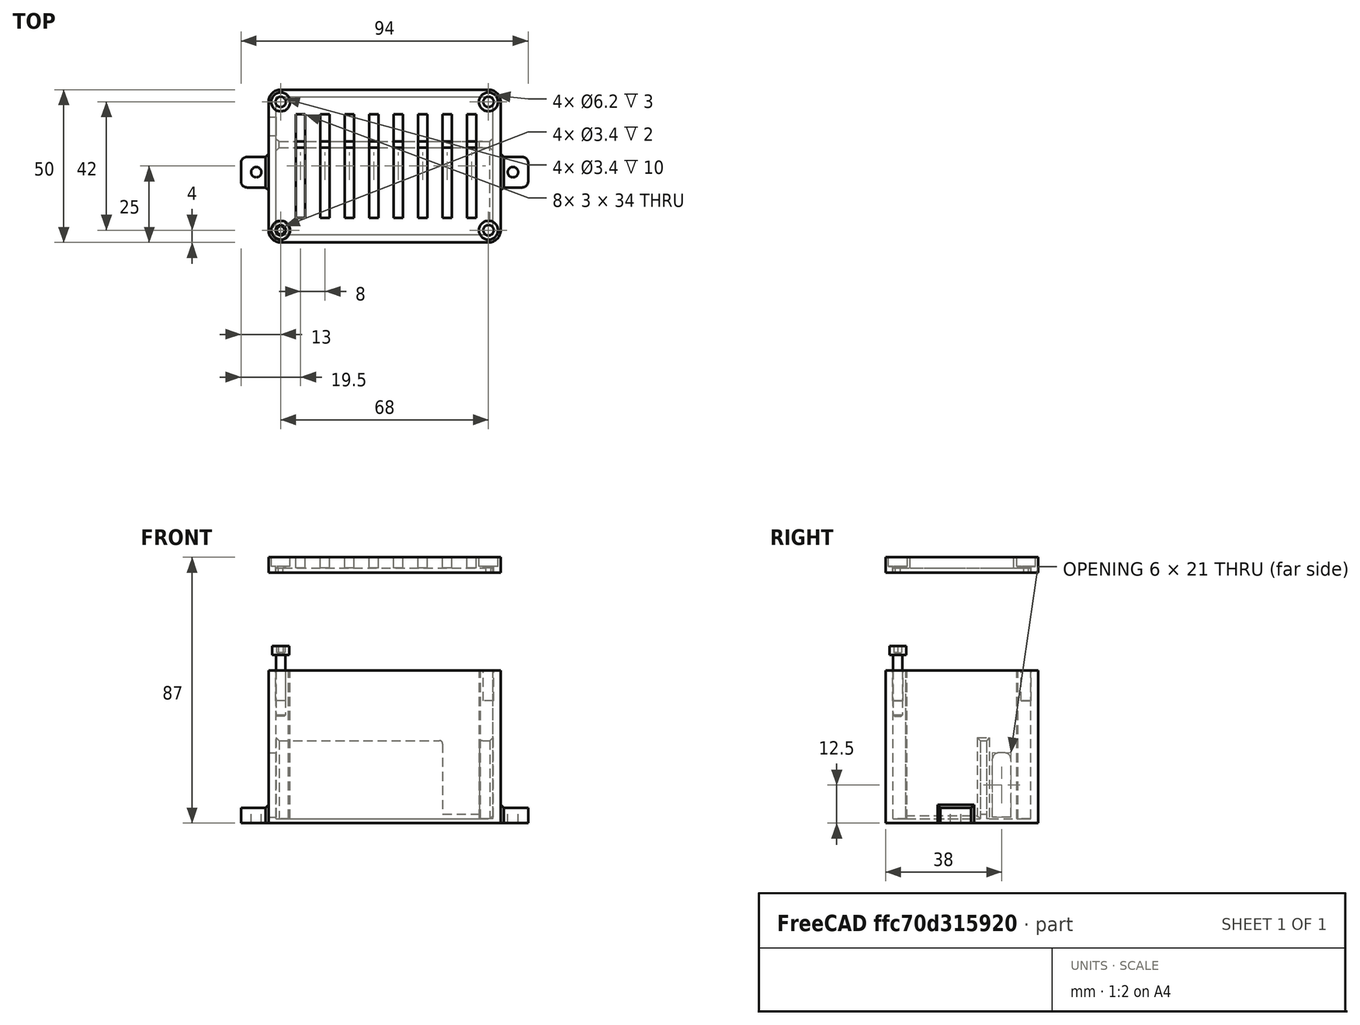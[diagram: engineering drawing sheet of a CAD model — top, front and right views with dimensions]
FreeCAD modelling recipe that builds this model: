
FCSTD DOCUMENT  (FreeCAD 0.17R12831 (Git))
Label: arbol_deseos_caja
License: All rights reserved
LicenseURL: http://es.wikipedia.org/wiki/Todos_los_derechos_reservados
objects: Part::Cylinder×18, Part::Box×17, Part::Cut×10, Part::MultiFuse×7, Part::Chamfer×4, Part::Fillet×3
note: 59 computed .brp shape members not serialized (recipe doc carries the construction recipe); baked Part::Feature solids carry a one-line shape summary decoded from their .brp

FEATURE [Part::Box] Box  label="caja exterior"
  AttacherType = Attacher::AttachEngine3D
  Height = 50
  Length = 76
  Placement = pos=(-1,-1,0) rot=(0,0,1;0rad)
  Width = 50
FEATURE [Part::Box] Box001  label="vaciado interior"
  AttacherType = Attacher::AttachEngine3D
  Height = 50
  Length = 71
  Placement = pos=(1.5,1.5,1.5) rot=(0,0,1;0rad)
  Width = 45
FEATURE [Part::Cut] Cut  label="parte inferior"
  Base = -> Box
  Tool = -> Box001
FEATURE [Part::Cylinder] Cylinder  label="soporte tornillo"
  Angle = 360
  AttacherType = Attacher::AttachEngine3D
  Height = 50
  Placement = pos=(3,3,0) rot=(0,0,1;0rad)
  Radius = 3
FEATURE [Part::Cylinder] Cylinder001  label="orificio tornillo"
  Angle = 360
  AttacherType = Attacher::AttachEngine3D
  Height = 10
  Placement = pos=(3,3,40) rot=(0,0,1;0rad)
  Radius = 1.7
FEATURE [Part::Box] Box002  label="separador"
  AttacherType = Attacher::AttachEngine3D
  Height = 27
  Length = 74
  Placement = pos=(0,30,0) rot=(0,0,1;0rad)
  Width = 2
FEATURE [Part::Chamfer] Chamfer001
  Edges = 2 edges r=0.1: [Edge6,Edge7]
  Placement = pos=(3,3,55) rot=(0,0,1;0rad)
FEATURE [Part::Cylinder] Cylinder002  label="soporte tornillo001"
  Angle = 360
  AttacherType = Attacher::AttachEngine3D
  Height = 50
  Placement = pos=(71,3,0) rot=(0,0,1;0rad)
  Radius = 3
FEATURE [Part::Cylinder] Cylinder003  label="orificio tornillo001"
  Angle = 360
  AttacherType = Attacher::AttachEngine3D
  Height = 10
  Placement = pos=(71,3,40) rot=(0,0,1;0rad)
  Radius = 1.7
FEATURE [Part::Cylinder] Cylinder004  label="soporte tornillo002"
  Angle = 360
  AttacherType = Attacher::AttachEngine3D
  Height = 50
  Placement = pos=(3,45,0) rot=(0,0,1;0rad)
  Radius = 3
FEATURE [Part::Cylinder] Cylinder005  label="orificio tornillo002"
  Angle = 360
  AttacherType = Attacher::AttachEngine3D
  Height = 10
  Placement = pos=(3,45,40) rot=(0,0,1;0rad)
  Radius = 1.7
FEATURE [Part::Cylinder] Cylinder006  label="soporte tornillo003"
  Angle = 360
  AttacherType = Attacher::AttachEngine3D
  Height = 50
  Placement = pos=(71,45,0) rot=(0,0,1;0rad)
  Radius = 3
FEATURE [Part::Cylinder] Cylinder007  label="orificio tornillo003"
  Angle = 360
  AttacherType = Attacher::AttachEngine3D
  Height = 10
  Placement = pos=(71,45,40) rot=(0,0,1;0rad)
  Radius = 1.7
FEATURE [Part::Box] Box003  label="entrada alimentacion"
  AttacherType = Attacher::AttachEngine3D
  Height = 21
  Length = 6
  Placement = pos=(-3,34,2) rot=(0,0,1;0rad)
  Width = 6
FEATURE [Part::Box] Box004  label="salida alimentacion para esp"
  AttacherType = Attacher::AttachEngine3D
  Height = 27
  Length = 12
  Placement = pos=(56,28,3) rot=(0,0,1;0rad)
  Width = 5
FEATURE [Part::Box] Box005  label="soporte exterior"
  AttacherType = Attacher::AttachEngine3D
  Height = 5
  Length = 10
  Placement = pos=(-10,17,0) rot=(0,0,1;0rad)
  Width = 10
FEATURE [Part::Cylinder] Cylinder008  label="orificio soporte exterior"
  Angle = 360
  AttacherType = Attacher::AttachEngine3D
  Height = 10
  Placement = pos=(-5,22,-1) rot=(0,0,1;0rad)
  Radius = 1.7
FEATURE [Part::Cut] Cut001  label="soporte exterior 1"
  Base = -> Box005
  Tool = -> Cylinder008
FEATURE [Part::Box] Box006  label="soporte exterior001"
  AttacherType = Attacher::AttachEngine3D
  Height = 5
  Length = 10
  Placement = pos=(-10,17,0) rot=(0,0,1;0rad)
  Width = 10
FEATURE [Part::Cylinder] Cylinder009  label="orificio soporte exterior001"
  Angle = 360
  AttacherType = Attacher::AttachEngine3D
  Height = 10
  Placement = pos=(-5,22,-1) rot=(0,0,1;0rad)
  Radius = 1.7
FEATURE [Part::Cut] Cut002  label="soporte exterior 002"
  Base = -> Box006
  Placement = pos=(84,0,0) rot=(0,0,1;0rad)
  Tool = -> Cylinder009
FEATURE [Part::MultiFuse] Fusion  label="soportes exteriores"
  Shapes = -> [Cut001,Cut002]
FEATURE [Part::MultiFuse] Fusion001  label="soportes tornillos"
  Shapes = -> [Cylinder,Cylinder002,Cylinder004,Cylinder006]
FEATURE [Part::MultiFuse] Fusion002  label="caja sin orificions"
  Shapes = -> [Box002,Cut,Fusion,Fusion001]
FEATURE [Part::MultiFuse] Fusion003  label="orificions tornillos"
  Shapes = -> [Cylinder001,Cylinder003,Cylinder005,Cylinder007]
FEATURE [Part::Cut] Cut003
  Base = -> Fusion002
  Tool = -> Fusion003
FEATURE [Part::Cut] Cut004
  Base = -> Cut003
  Tool = -> Box004
FEATURE [Part::Cut] Cut005
  Base = -> Cut004
  Tool = -> Box003
FEATURE [Part::Chamfer] Chamfer
  Base = -> Cut005
  Edges = 1 edges r=1: [Edge71]
FEATURE [Part::Chamfer] Chamfer002
  Base = -> Chamfer
  Edges = 1 edges r=1: [Edge61]
FEATURE [Part::Box] Box007  label="caja exterior001"
  AttacherType = Attacher::AttachEngine3D
  Height = 5
  Length = 76
  Placement = pos=(-1,-1,50) rot=(0,0,1;0rad)
  Width = 50
FEATURE [Part::Box] Box008  label="vaciado interior001"
  AttacherType = Attacher::AttachEngine3D
  Height = 5
  Length = 71
  Placement = pos=(1.5,1.5,46.5) rot=(0,0,1;0rad)
  Width = 45
FEATURE [Part::Cut] Cut006  label="tapa superior"
  Base = -> Box007
  Tool = -> Box008
FEATURE [Part::Fillet] Fillet006
  Base = -> Cut006
  Edges = 4 edges r=4: [Edge1,Edge3,Edge6,Edge11]
FEATURE [Part::Cylinder] Cylinder010  label="orificio tornillo004"
  Angle = 360
  AttacherType = Attacher::AttachEngine3D
  Height = 10
  Placement = pos=(71,3,40) rot=(0,0,1;0rad)
  Radius = 1.7
FEATURE [Part::Cylinder] Cylinder011  label="orificio tornillo005"
  Angle = 360
  AttacherType = Attacher::AttachEngine3D
  Height = 10
  Placement = pos=(71,45,40) rot=(0,0,1;0rad)
  Radius = 1.7
FEATURE [Part::Cylinder] Cylinder012  label="orificio tornillo006"
  Angle = 360
  AttacherType = Attacher::AttachEngine3D
  Height = 10
  Placement = pos=(3,3,40) rot=(0,0,1;0rad)
  Radius = 1.7
FEATURE [Part::Cylinder] Cylinder013  label="orificio tornillo007"
  Angle = 360
  AttacherType = Attacher::AttachEngine3D
  Height = 10
  Placement = pos=(3,45,40) rot=(0,0,1;0rad)
  Radius = 1.7
FEATURE [Part::MultiFuse] Fusion004  label="orificions tornillos001"
  Placement = pos=(0,0,6) rot=(0,0,1;0rad)
  Shapes = -> [Cylinder012,Cylinder010,Cylinder013,Cylinder011]
FEATURE [Part::Cylinder] Cylinder014  label="orificio tornillo008"
  Angle = 360
  AttacherType = Attacher::AttachEngine3D
  Height = 3
  Placement = pos=(3,3,40) rot=(0,0,1;0rad)
  Radius = 3.1
FEATURE [Part::Cylinder] Cylinder015  label="orificio tornillo009"
  Angle = 360
  AttacherType = Attacher::AttachEngine3D
  Height = 3
  Placement = pos=(71,3,40) rot=(0,0,1;0rad)
  Radius = 3.1
FEATURE [Part::Cylinder] Cylinder016  label="orificio tornillo010"
  Angle = 360
  AttacherType = Attacher::AttachEngine3D
  Height = 3
  Placement = pos=(71,45,40) rot=(0,0,1;0rad)
  Radius = 3.1
FEATURE [Part::Cylinder] Cylinder017  label="orificio tornillo011"
  Angle = 360
  AttacherType = Attacher::AttachEngine3D
  Height = 3
  Placement = pos=(3,45,40) rot=(0,0,1;0rad)
  Radius = 3.1
FEATURE [Part::MultiFuse] Fusion005  label="orificions cabezas superior"
  Placement = pos=(0,0,12) rot=(0,0,1;0rad)
  Shapes = -> [Cylinder014,Cylinder015,Cylinder017,Cylinder016]
FEATURE [Part::Cut] Cut007
  Base = -> Fillet006
  Tool = -> Fusion004
FEATURE [Part::Cut] Cut008
  Base = -> Cut007
  Tool = -> Fusion005
FEATURE [Part::Box] Box009  label="Cubo"
  AttacherType = Attacher::AttachEngine3D
  Height = 15
  Length = 3
  Placement = pos=(8,7,46) rot=(0,0,1;0rad)
  Width = 34
FEATURE [Part::Box] Box010  label="Cubo001"
  AttacherType = Attacher::AttachEngine3D
  Height = 15
  Length = 3
  Placement = pos=(16,7,46) rot=(0,0,1;0rad)
  Width = 34
FEATURE [Part::Box] Box011  label="Cubo002"
  AttacherType = Attacher::AttachEngine3D
  Height = 15
  Length = 3
  Placement = pos=(24,7,46) rot=(0,0,1;0rad)
  Width = 34
FEATURE [Part::Box] Box012  label="Cubo003"
  AttacherType = Attacher::AttachEngine3D
  Height = 15
  Length = 3
  Placement = pos=(32,7,46) rot=(0,0,1;0rad)
  Width = 34
FEATURE [Part::Box] Box013  label="Cubo004"
  AttacherType = Attacher::AttachEngine3D
  Height = 15
  Length = 3
  Placement = pos=(40,7,46) rot=(0,0,1;0rad)
  Width = 34
FEATURE [Part::Box] Box014  label="Cubo005"
  AttacherType = Attacher::AttachEngine3D
  Height = 15
  Length = 3
  Placement = pos=(48,7,46) rot=(0,0,1;0rad)
  Width = 34
FEATURE [Part::Box] Box015  label="Cubo006"
  AttacherType = Attacher::AttachEngine3D
  Height = 15
  Length = 3
  Placement = pos=(56,7,46) rot=(0,0,1;0rad)
  Width = 34
FEATURE [Part::Box] Box016  label="Cubo007"
  AttacherType = Attacher::AttachEngine3D
  Height = 15
  Length = 3
  Placement = pos=(64,7,46) rot=(0,0,1;0rad)
  Width = 34
FEATURE [Part::MultiFuse] Fusion006
  Shapes = -> [Box009,Box010,Box016,Box013,Box015,Box012,Box014,Box011]
FEATURE [Part::Cut] Cut009  label="tapa superior completa"
  Base = -> Cut008
  Placement = pos=(0,0,32) rot=(0,0,1;0rad)
  Tool = -> Fusion006
FEATURE [Part::Fillet] Fillet
  Base = -> Chamfer002
  Edges = 4 edges r=4: [Edge3,Edge7,Edge29,Edge51]
FEATURE [Part::Chamfer] Chamfer003
  Base = -> Fillet
  Edges = 11 edges r=1: [Edge7,Edge9,Edge73,Edge74,Edge75,Edge91,Edge93,Edge95,Edge112,Edge113,Edge115]
FEATURE [Part::Fillet] Fillet007  label="parte inferior001"
  Base = -> Chamfer003
  Edges = 8 edges: [Edge66 r=2,Edge68 r=2,Edge80 r=2,Edge82 r=2,Edge87 r=2,Edge90 r=2,Edge156 r=1,Edge161 r=1]
